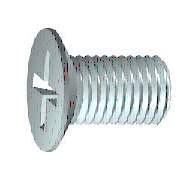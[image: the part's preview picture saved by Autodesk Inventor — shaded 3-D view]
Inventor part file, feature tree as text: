
AUTODESK INVENTOR PART (.ipt)
format: ipt  version: 2017 (Build 210142000, 142)  size: 242,688 bytes
history: native  units: mm (DEFAULTED — no unit token found)
features: sketch x2, other x1, extrude x1, plane x1
ambient origin geometry x7: Origin, YZ Plane, XZ Plane, X Axis, Y Axis, Z Axis, Center Point
bodies: Solid1 (feature_tree)
feature tree (5):
  sketch  "Esquisse1"
  other  "Corps"
  extrude  "Rainure"  Depth=7.35mm
  plane  "Work Plane2"
  sketch  "Esquisse2"
